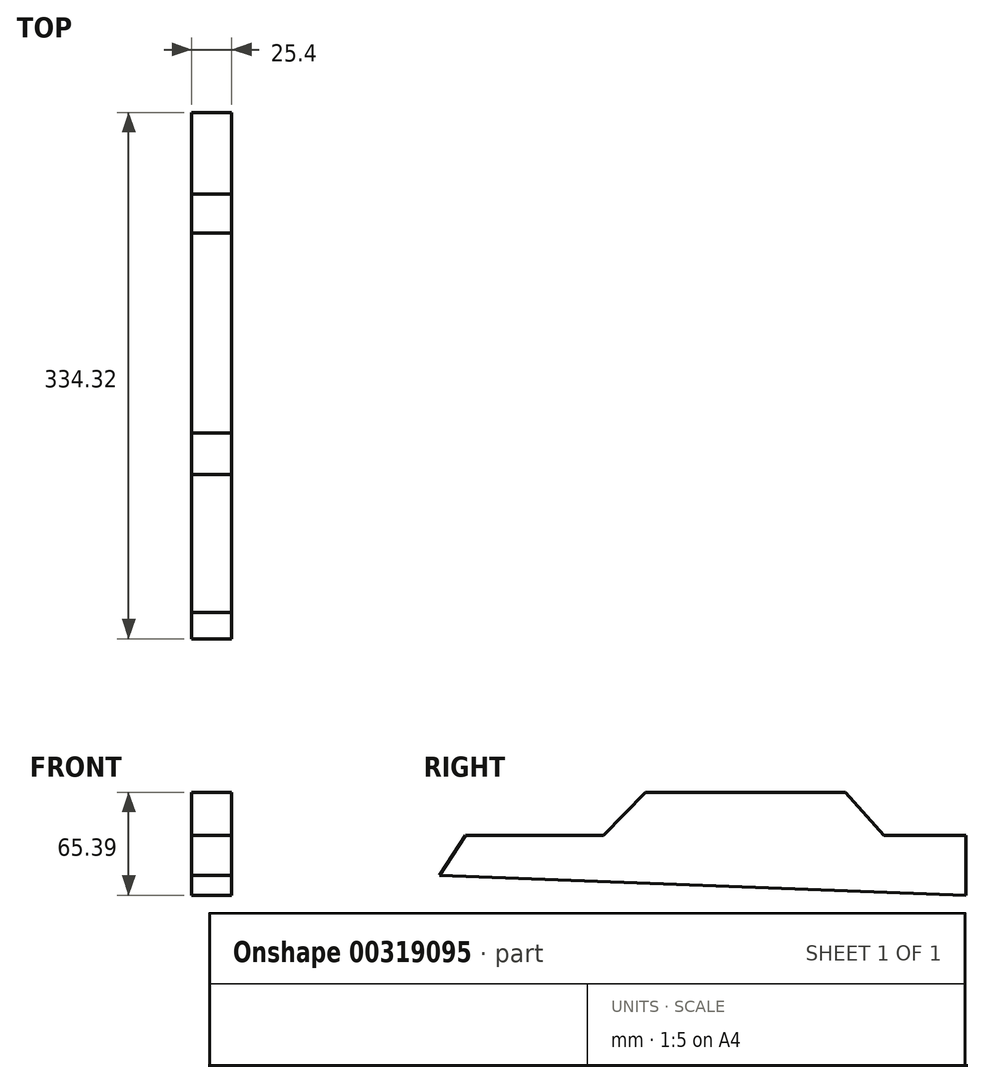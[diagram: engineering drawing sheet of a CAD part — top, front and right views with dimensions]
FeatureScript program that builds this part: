
annotation { "Feature Type Name" : "Feature", "Feature Type Description" : "" }
export const myFeature = defineFeature(function(context is Context, id is Id, definition is map)
    precondition{}
    {
        {
            var Q0;
            Q0=qCreatedBy(makeId("Right.planeOp"),FACE);
            var sketch = newSketch(context, id + "F0", { "sketchPlane" : qUnion([Q0])});
            skLineSegment(sketch, "E0", {"start": v(-136.03, -22.17) * mm, "end": v(-48.47, -22.17) * mm});
            skLineSegment(sketch, "E1", {"start": v(-48.47, -22.17) * mm, "end": v(-21.89, 5.12) * mm});
            skLineSegment(sketch, "E2", {"start": v(-21.89, 5.12) * mm, "end": v(105.11, 5.12) * mm});
            skLineSegment(sketch, "E3", {"start": v(105.11, 5.12) * mm, "end": v(129.64, -22.17) * mm});
            skLineSegment(sketch, "E4", {"start": v(129.64, -22.17) * mm, "end": v(181.61, -22.17) * mm});
            skLineSegment(sketch, "E5", {"start": v(181.61, -22.17) * mm, "end": v(181.61, -60.27) * mm});
            skLineSegment(sketch, "E6", {"start": v(-136.03, -22.17) * mm, "end": v(-152.71, -47.69) * mm});
            skLineSegment(sketch, "E7", {"start": v(-152.71, -47.69) * mm, "end": v(181.61, -60.27) * mm});
            skSolve(sketch);
        }
        {
            var Q0;
            Q0=makeQuery(id+"F0.imprint","IMPRINT",FACE,{"disambiguationData":[TD([[makeQuery(id+"F0.imprint","IMPRINT",EDGE,{"derivedFrom":sQuery(id+"F0.wireOp",EDGE,"E0")}),-1.0]])]});
            extrude(context, id + "F1", {"entities" : qUnion([Q0]), "depth" : 25.4 * mm});
        }
    });
